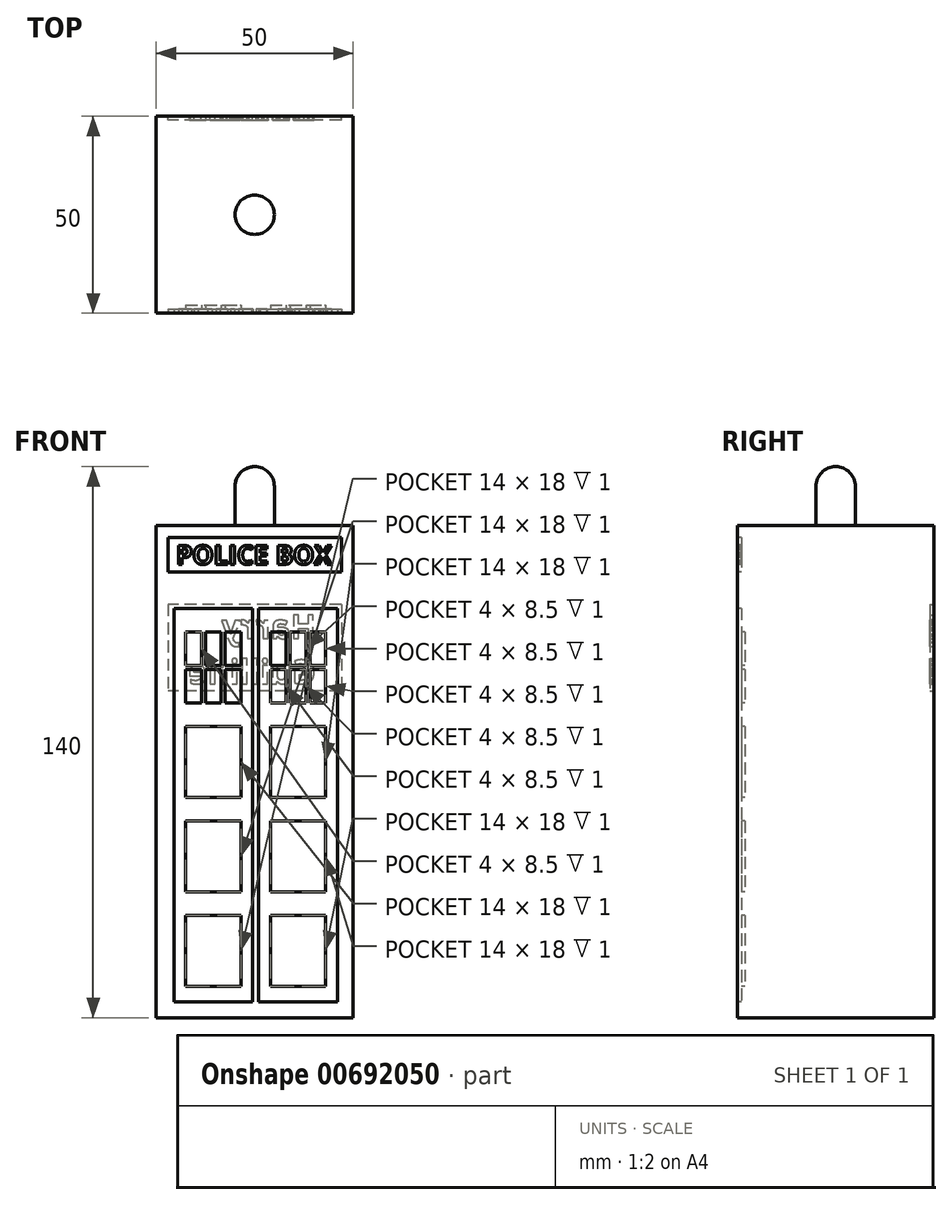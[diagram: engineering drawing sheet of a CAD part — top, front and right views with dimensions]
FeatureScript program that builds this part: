
annotation { "Feature Type Name" : "Feature", "Feature Type Description" : "" }
export const myFeature = defineFeature(function(context is Context, id is Id, definition is map)
    precondition{}
    {
        {
            var Q0;
            Q0=qCreatedBy(makeId("Top.planeOp"),FACE);
            var sketch = newSketch(context, id + "F0", { "sketchPlane" : qUnion([Q0])});
            skLineSegment(sketch, "E0.bottom", {"start": v(-25, 25) * mm, "end": v(25, 25) * mm});
            skLineSegment(sketch, "E0.top", {"start": v(-25, -25) * mm, "end": v(25, -25) * mm});
            skLineSegment(sketch, "E0.left", {"start": v(-25, 25) * mm, "end": v(-25, -25) * mm});
            skLineSegment(sketch, "E0.right", {"start": v(25, 25) * mm, "end": v(25, -25) * mm});
            skSolve(sketch);
        }
        {
            var Q0;
            Q0 = qSketchRegion(id + "F0", true);
            extrude(context, id + "F1", {"entities" : qUnion([Q0]), "depth" : 125 * mm, "offsetDistance" : 25 * mm});
        }
        {
            var Q0;
            Q0=makeQuery(id+"F1.opExtrude","CAP_FACE",FACE,{"disambiguationData":[OSD([sQuery(id+"F0.wireOp",EDGE,"E0.bottom"),sQuery(id+"F0.wireOp",EDGE,"E0.top"),sQuery(id+"F0.wireOp",EDGE,"E0.left"),sQuery(id+"F0.wireOp",EDGE,"E0.right")])],"isStart":false});
            cPlane(context, id + "F2", {"entities" : qUnion([Q0]), "cplaneType" : CPlaneType.OFFSET, "offset" : 0 * mm, "width" : 150 * mm, "height" : 150 * mm});
        }
        {
            var Q0;
            Q0=qCreatedBy(makeId("Front.planeOp"),FACE);
            var sketch = newSketch(context, id + "F3", { "sketchPlane" : qUnion([Q0])});
            skLineSegment(sketch, "E1", {"start": v(0, -12.11) * mm, "end": v(0, 144.87) * mm, "construction": true});
            skArc(sketch, "E2", {"start": v(0, 140) * mm, "mid": v(-3.54, 138.54) * mm, "end": v(-5, 135) * mm});
            skLineSegment(sketch, "E3.0.0", {"start": v(-25, 0) * mm, "end": v(25, 0) * mm});
            skLineSegment(sketch, "E3.0.1", {"start": v(25, 0) * mm, "end": v(25, 125) * mm});
            skLineSegment(sketch, "E3.0.2", {"start": v(25, 125) * mm, "end": v(-25, 125) * mm});
            skLineSegment(sketch, "E3.0.3", {"start": v(-25, 125) * mm, "end": v(-25, 0) * mm});
            skLineSegment(sketch, "E4", {"start": v(-5, 135) * mm, "end": v(-5, 125) * mm});
            skLineSegment(sketch, "E5", {"start": v(0, 140) * mm, "end": v(0, 125) * mm});
            skSolve(sketch);
        }
        {
            var Q0;
            Q0=makeQuery(id+"F3.imprint","IMPRINT",FACE,{"disambiguationData":[TD([[makeQuery(id+"F3.imprint","IMPRINT",EDGE,{"derivedFrom":sQuery(id+"F3.wireOp",EDGE,"E2")}),1.0]])]});
            var Q1;
            Q1=sQuery(id+"F3.wireOp",EDGE,"E1");
            revolve(context, id + "F4", {"operationType" : NewBodyOperationType.ADD, "entities" : qUnion([Q0]), "axis" : qUnion([Q1]), "revolveType" : RevolveType.FULL});
        }
        {
            var Q0;
            Q0=makeQuery(id+"F1.opExtrude","SWEPT_FACE",FACE,{"disambiguationData":[OSD([sQuery(id+"F0.wireOp",EDGE,"E0.top")])]});
            cPlane(context, id + "F5", {"entities" : qUnion([Q0]), "cplaneType" : CPlaneType.OFFSET, "offset" : 0 * mm, "width" : 150 * mm, "height" : 150 * mm});
        }
        {
            var Q0;
            Q0=qCreatedBy(id+"F5.planeOp",FACE);
            var sketch = newSketch(context, id + "F6", { "sketchPlane" : qUnion([Q0])});
            skLineSegment(sketch, "E6", {"start": v(0, -21.96) * mm, "end": v(0, 160.1) * mm, "construction": true});
            skLineSegment(sketch, "E7.bottom", {"start": v(-22, 122) * mm, "end": v(22, 122) * mm});
            skLineSegment(sketch, "E7.top", {"start": v(-22, 113.18) * mm, "end": v(22, 113.18) * mm});
            skLineSegment(sketch, "E7.left", {"start": v(-22, 122) * mm, "end": v(-22, 113.18) * mm});
            skLineSegment(sketch, "E7.right", {"start": v(22, 122) * mm, "end": v(22, 113.18) * mm});
            skLineSegment(sketch, "E8.0", {"start": v(-25, 125) * mm, "end": v(-25, 0) * mm});
            skLineSegment(sketch, "E9.0", {"start": v(-25, 125) * mm, "end": v(25, 125) * mm});
            skLineSegment(sketch, "E10.0", {"start": v(25, 125) * mm, "end": v(25, 0) * mm});
            skText(sketch, "E11", { "text": "POLICE BOX", "fontName": "OpenSans-Bold.ttf"});
            skLineSegment(sketch, "E12.bottom", {"start": v(1, 104) * mm, "end": v(21, 104) * mm});
            skLineSegment(sketch, "E12.top", {"start": v(1, 4) * mm, "end": v(21, 4) * mm});
            skLineSegment(sketch, "E12.left", {"start": v(1, 104) * mm, "end": v(1, 4) * mm});
            skLineSegment(sketch, "E12.right", {"start": v(21, 104) * mm, "end": v(21, 4) * mm});
            skLineSegment(sketch, "E13.bottom", {"start": v(4, 98) * mm, "end": v(18, 98) * mm});
            skLineSegment(sketch, "E13.top", {"start": v(4, 80) * mm, "end": v(18, 80) * mm});
            skLineSegment(sketch, "E13.left", {"start": v(4, 98) * mm, "end": v(4, 80) * mm});
            skLineSegment(sketch, "E13.right", {"start": v(18, 98) * mm, "end": v(18, 80) * mm});
            skLineSegment(sketch, "E14.bottom", {"start": v(4, 74) * mm, "end": v(18, 74) * mm});
            skLineSegment(sketch, "E14.top", {"start": v(4, 56) * mm, "end": v(18, 56) * mm});
            skLineSegment(sketch, "E14.left", {"start": v(4, 74) * mm, "end": v(4, 56) * mm});
            skLineSegment(sketch, "E14.right", {"start": v(18, 74) * mm, "end": v(18, 56) * mm});
            skLineSegment(sketch, "E15.bottom", {"start": v(4, 50) * mm, "end": v(18, 50) * mm});
            skLineSegment(sketch, "E15.top", {"start": v(4, 32) * mm, "end": v(18, 32) * mm});
            skLineSegment(sketch, "E15.left", {"start": v(4, 50) * mm, "end": v(4, 32) * mm});
            skLineSegment(sketch, "E15.right", {"start": v(18, 50) * mm, "end": v(18, 32) * mm});
            skLineSegment(sketch, "E16.bottom", {"start": v(4, 26) * mm, "end": v(18, 26) * mm});
            skLineSegment(sketch, "E16.top", {"start": v(4, 8) * mm, "end": v(18, 8) * mm});
            skLineSegment(sketch, "E16.left", {"start": v(4, 26) * mm, "end": v(4, 8) * mm});
            skLineSegment(sketch, "E16.right", {"start": v(18, 26) * mm, "end": v(18, 8) * mm});
            skLineSegment(sketch, "E17", {"start": v(4, 89.5) * mm, "end": v(8, 89.5) * mm});
            skLineSegment(sketch, "E18", {"start": v(4, 88.5) * mm, "end": v(8, 88.5) * mm});
            skLineSegment(sketch, "E19", {"start": v(8, 98) * mm, "end": v(8, 89.5) * mm});
            skLineSegment(sketch, "E20", {"start": v(9, 98) * mm, "end": v(9, 89.5) * mm});
            skLineSegment(sketch, "E21", {"start": v(13, 98) * mm, "end": v(13, 89.5) * mm});
            skLineSegment(sketch, "E22", {"start": v(14, 98) * mm, "end": v(14, 89.5) * mm});
            skLineSegment(sketch, "E23.trimOffspring", {"start": v(9, 88.5) * mm, "end": v(13, 88.5) * mm});
            skLineSegment(sketch, "E24.trimOffspring", {"start": v(9, 89.5) * mm, "end": v(13, 89.5) * mm});
            skLineSegment(sketch, "E25.trimOffspring", {"start": v(8, 88.5) * mm, "end": v(8, 80) * mm});
            skLineSegment(sketch, "E26.trimOffspring", {"start": v(9, 88.5) * mm, "end": v(9, 80) * mm});
            skLineSegment(sketch, "E27.trimOffspring", {"start": v(13, 88.5) * mm, "end": v(13, 80) * mm});
            skLineSegment(sketch, "E28.trimOffspring", {"start": v(14, 88.5) * mm, "end": v(14, 80) * mm});
            skLineSegment(sketch, "E29.trimOffspring", {"start": v(14, 89.5) * mm, "end": v(18, 89.5) * mm});
            skLineSegment(sketch, "E30.trimOffspring", {"start": v(14, 88.5) * mm, "end": v(18, 88.5) * mm});
            skLineSegment(sketch, "E31", {"start": v(-21.5, -74.33) * mm, "end": v(-21.5, 107.73) * mm, "construction": true});
            skLineSegment(sketch, "E32.bottom", {"start": v(-20.5, 104) * mm, "end": v(-0.5, 104) * mm});
            skLineSegment(sketch, "E32.top", {"start": v(-20.5, 4) * mm, "end": v(-0.5, 4) * mm});
            skLineSegment(sketch, "E32.left", {"start": v(-20.5, 104) * mm, "end": v(-20.5, 4) * mm});
            skLineSegment(sketch, "E32.right", {"start": v(-0.5, 104) * mm, "end": v(-0.5, 4) * mm});
            skLineSegment(sketch, "E33.bottom", {"start": v(-17.5, 98) * mm, "end": v(-3.5, 98) * mm});
            skLineSegment(sketch, "E33.top", {"start": v(-17.5, 80) * mm, "end": v(-3.5, 80) * mm});
            skLineSegment(sketch, "E33.left", {"start": v(-17.5, 98) * mm, "end": v(-17.5, 80) * mm});
            skLineSegment(sketch, "E33.right", {"start": v(-3.5, 98) * mm, "end": v(-3.5, 80) * mm});
            skLineSegment(sketch, "E34.bottom", {"start": v(-17.5, 74) * mm, "end": v(-3.5, 74) * mm});
            skLineSegment(sketch, "E34.top", {"start": v(-17.5, 56) * mm, "end": v(-3.5, 56) * mm});
            skLineSegment(sketch, "E34.left", {"start": v(-17.5, 74) * mm, "end": v(-17.5, 56) * mm});
            skLineSegment(sketch, "E34.right", {"start": v(-3.5, 74) * mm, "end": v(-3.5, 56) * mm});
            skLineSegment(sketch, "E35.bottom", {"start": v(-17.5, 50) * mm, "end": v(-3.5, 50) * mm});
            skLineSegment(sketch, "E35.top", {"start": v(-17.5, 32) * mm, "end": v(-3.5, 32) * mm});
            skLineSegment(sketch, "E35.left", {"start": v(-17.5, 50) * mm, "end": v(-17.5, 32) * mm});
            skLineSegment(sketch, "E35.right", {"start": v(-3.5, 50) * mm, "end": v(-3.5, 32) * mm});
            skLineSegment(sketch, "E36.bottom", {"start": v(-17.5, 26) * mm, "end": v(-3.5, 26) * mm});
            skLineSegment(sketch, "E36.top", {"start": v(-17.5, 8) * mm, "end": v(-3.5, 8) * mm});
            skLineSegment(sketch, "E36.left", {"start": v(-17.5, 26) * mm, "end": v(-17.5, 8) * mm});
            skLineSegment(sketch, "E36.right", {"start": v(-3.5, 26) * mm, "end": v(-3.5, 8) * mm});
            skLineSegment(sketch, "E37", {"start": v(-17.5, 89.5) * mm, "end": v(-13.5, 89.5) * mm});
            skLineSegment(sketch, "E38", {"start": v(-17.5, 88.5) * mm, "end": v(-13.5, 88.5) * mm});
            skLineSegment(sketch, "E39", {"start": v(-13.5, 98) * mm, "end": v(-13.5, 89.5) * mm});
            skLineSegment(sketch, "E40", {"start": v(-12.5, 98) * mm, "end": v(-12.5, 89.5) * mm});
            skLineSegment(sketch, "E41", {"start": v(-8.5, 98) * mm, "end": v(-8.5, 89.5) * mm});
            skLineSegment(sketch, "E42", {"start": v(-7.5, 98) * mm, "end": v(-7.5, 89.5) * mm});
            skLineSegment(sketch, "E43.trimOffspring", {"start": v(-12.5, 88.5) * mm, "end": v(-8.5, 88.5) * mm});
            skLineSegment(sketch, "E44.trimOffspring", {"start": v(-12.5, 89.5) * mm, "end": v(-8.5, 89.5) * mm});
            skLineSegment(sketch, "E45.trimOffspring", {"start": v(-13.5, 88.5) * mm, "end": v(-13.5, 80) * mm});
            skLineSegment(sketch, "E46.trimOffspring", {"start": v(-12.5, 88.5) * mm, "end": v(-12.5, 80) * mm});
            skLineSegment(sketch, "E47.trimOffspring", {"start": v(-8.5, 88.5) * mm, "end": v(-8.5, 80) * mm});
            skLineSegment(sketch, "E48.trimOffspring", {"start": v(-7.5, 88.5) * mm, "end": v(-7.5, 80) * mm});
            skLineSegment(sketch, "E49.trimOffspring", {"start": v(-7.5, 89.5) * mm, "end": v(-3.5, 89.5) * mm});
            skLineSegment(sketch, "E50.trimOffspring", {"start": v(-7.5, 88.5) * mm, "end": v(-3.5, 88.5) * mm});
            const initialGuessF6  = {"E11": [-0.02, 0.11518, 1, 0, 0.00482]};
            skSetInitialGuess(sketch, initialGuessF6);
            skSolve(sketch);
        }
        {
            var Q0;
            Q0=makeQuery(id+"F6.imprint","IMPRINT",FACE,{"disambiguationData":[TD([[makeQuery(id+"F6.imprint","IMPRINT",EDGE,{"derivedFrom":sQuery(id+"F6.wireOp",EDGE,"E7.bottom")}),-1.0]])]});
            var Q1;
            Q1=makeQuery(id+"F6.imprint","IMPRINT",FACE,{"disambiguationData":[TD([[makeQuery(id+"F6.imprint","IMPRINT",EDGE,{"derivedFrom":sQuery(id+"F6.wireOp",EDGE,"E11.sketch_text.stroke-24")}),1.0]])]});
            var Q2;
            Q2=makeQuery(id+"F6.imprint","IMPRINT",FACE,{"disambiguationData":[TD([[makeQuery(id+"F6.imprint","IMPRINT",EDGE,{"derivedFrom":sQuery(id+"F6.wireOp",EDGE,"E11.sketch_text.stroke-0")}),1.0]])]});
            var Q3;
            Q3=makeQuery(id+"F6.imprint","IMPRINT",FACE,{"disambiguationData":[TD([[makeQuery(id+"F6.imprint","IMPRINT",EDGE,{"derivedFrom":sQuery(id+"F6.wireOp",EDGE,"E11.sketch_text.stroke-100")}),1.0]])]});
            var Q4;
            Q4=makeQuery(id+"F6.imprint","IMPRINT",FACE,{"disambiguationData":[TD([[makeQuery(id+"F6.imprint","IMPRINT",EDGE,{"derivedFrom":sQuery(id+"F6.wireOp",EDGE,"E11.sketch_text.stroke-79")}),1.0]])]});
            var Q5;
            Q5=makeQuery(id+"F6.imprint","IMPRINT",FACE,{"disambiguationData":[TD([[makeQuery(id+"F6.imprint","IMPRINT",EDGE,{"derivedFrom":sQuery(id+"F6.wireOp",EDGE,"E11.sketch_text.stroke-86")}),1.0]])]});
            extrude(context, id + "F7", {"entities" : qUnion([Q0, Q1, Q2, Q3, Q4, Q5]), "operationType" : NewBodyOperationType.REMOVE, "oppositeDirection" : true, "depth" : 1 * mm, "offsetDistance" : 25 * mm});
        }
        {
            var Q0;
            {var subQ4=sQuery(id+"F6.wireOp",EDGE,"E37");Q0=makeQuery(id+"F6.imprint","IMPRINT",FACE,{"disambiguationData":[TD([[makeQuery(id+"F6.imprint","IMPRINT",EDGE,{"derivedFrom":subQ4}),1.0]])]});}
            var Q1;
            {var subQ0=sQuery(id+"F6.wireOp",EDGE,"E40");Q1=makeQuery(id+"F6.imprint","IMPRINT",FACE,{"disambiguationData":[TD([[makeQuery(id+"F6.imprint","IMPRINT",EDGE,{"derivedFrom":subQ0}),1.0]])]});}
            var Q2;
            {var subQ3=sQuery(id+"F6.wireOp",EDGE,"E42");Q2=makeQuery(id+"F6.imprint","IMPRINT",FACE,{"disambiguationData":[TD([[makeQuery(id+"F6.imprint","IMPRINT",EDGE,{"derivedFrom":subQ3}),1.0]])]});}
            var Q3;
            {var subQ4=sQuery(id+"F6.wireOp",EDGE,"E17");Q3=makeQuery(id+"F6.imprint","IMPRINT",FACE,{"disambiguationData":[TD([[makeQuery(id+"F6.imprint","IMPRINT",EDGE,{"derivedFrom":subQ4}),1.0]])]});}
            var Q4;
            {var subQ0=sQuery(id+"F6.wireOp",EDGE,"E20");Q4=makeQuery(id+"F6.imprint","IMPRINT",FACE,{"disambiguationData":[TD([[makeQuery(id+"F6.imprint","IMPRINT",EDGE,{"derivedFrom":subQ0}),1.0]])]});}
            var Q5;
            {var subQ3=sQuery(id+"F6.wireOp",EDGE,"E22");Q5=makeQuery(id+"F6.imprint","IMPRINT",FACE,{"disambiguationData":[TD([[makeQuery(id+"F6.imprint","IMPRINT",EDGE,{"derivedFrom":subQ3}),1.0]])]});}
            var Q6;
            {var subQ3=sQuery(id+"F6.wireOp",EDGE,"E28.trimOffspring");Q6=makeQuery(id+"F6.imprint","IMPRINT",FACE,{"disambiguationData":[TD([[makeQuery(id+"F6.imprint","IMPRINT",EDGE,{"derivedFrom":subQ3}),1.0]])]});}
            var Q7;
            Q7=makeQuery(id+"F6.imprint","IMPRINT",FACE,{"disambiguationData":[TD([[makeQuery(id+"F6.imprint","IMPRINT",EDGE,{"derivedFrom":sQuery(id+"F6.wireOp",EDGE,"E23.trimOffspring")}),-1.0]])]});
            var Q8;
            {var subQ4=sQuery(id+"F6.wireOp",EDGE,"E18");Q8=makeQuery(id+"F6.imprint","IMPRINT",FACE,{"disambiguationData":[TD([[makeQuery(id+"F6.imprint","IMPRINT",EDGE,{"derivedFrom":subQ4}),-1.0]])]});}
            var Q9;
            {var subQ3=sQuery(id+"F6.wireOp",EDGE,"E48.trimOffspring");Q9=makeQuery(id+"F6.imprint","IMPRINT",FACE,{"disambiguationData":[TD([[makeQuery(id+"F6.imprint","IMPRINT",EDGE,{"derivedFrom":subQ3}),1.0]])]});}
            var Q10;
            Q10=makeQuery(id+"F6.imprint","IMPRINT",FACE,{"disambiguationData":[TD([[makeQuery(id+"F6.imprint","IMPRINT",EDGE,{"derivedFrom":sQuery(id+"F6.wireOp",EDGE,"E43.trimOffspring")}),-1.0]])]});
            var Q11;
            {var subQ4=sQuery(id+"F6.wireOp",EDGE,"E38");Q11=makeQuery(id+"F6.imprint","IMPRINT",FACE,{"disambiguationData":[TD([[makeQuery(id+"F6.imprint","IMPRINT",EDGE,{"derivedFrom":subQ4}),-1.0]])]});}
            var Q12;
            Q12=makeQuery(id+"F6.imprint","IMPRINT",FACE,{"disambiguationData":[TD([[makeQuery(id+"F6.imprint","IMPRINT",EDGE,{"derivedFrom":sQuery(id+"F6.wireOp",EDGE,"E34.bottom")}),-1.0]])]});
            var Q13;
            Q13=makeQuery(id+"F6.imprint","IMPRINT",FACE,{"disambiguationData":[TD([[makeQuery(id+"F6.imprint","IMPRINT",EDGE,{"derivedFrom":sQuery(id+"F6.wireOp",EDGE,"E14.bottom")}),-1.0]])]});
            var Q14;
            Q14=makeQuery(id+"F6.imprint","IMPRINT",FACE,{"disambiguationData":[TD([[makeQuery(id+"F6.imprint","IMPRINT",EDGE,{"derivedFrom":sQuery(id+"F6.wireOp",EDGE,"E35.bottom")}),-1.0]])]});
            var Q15;
            Q15=makeQuery(id+"F6.imprint","IMPRINT",FACE,{"disambiguationData":[TD([[makeQuery(id+"F6.imprint","IMPRINT",EDGE,{"derivedFrom":sQuery(id+"F6.wireOp",EDGE,"E15.bottom")}),-1.0]])]});
            var Q16;
            Q16=makeQuery(id+"F6.imprint","IMPRINT",FACE,{"disambiguationData":[TD([[makeQuery(id+"F6.imprint","IMPRINT",EDGE,{"derivedFrom":sQuery(id+"F6.wireOp",EDGE,"E36.bottom")}),-1.0]])]});
            var Q17;
            Q17=makeQuery(id+"F6.imprint","IMPRINT",FACE,{"disambiguationData":[TD([[makeQuery(id+"F6.imprint","IMPRINT",EDGE,{"derivedFrom":sQuery(id+"F6.wireOp",EDGE,"E16.bottom")}),-1.0]])]});
            extrude(context, id + "F8", {"entities" : qUnion([Q0, Q1, Q2, Q3, Q4, Q5, Q6, Q7, Q8, Q9, Q10, Q11, Q12, Q13, Q14, Q15, Q16, Q17]), "operationType" : NewBodyOperationType.REMOVE, "oppositeDirection" : true, "depth" : 2 * mm, "offsetDistance" : 25 * mm});
        }
        {
            var Q0;
            Q0=makeQuery(id+"F6.imprint","IMPRINT",FACE,{"disambiguationData":[TD([[makeQuery(id+"F6.imprint","IMPRINT",EDGE,{"derivedFrom":sQuery(id+"F6.wireOp",EDGE,"E32.bottom")}),-1.0]])]});
            var Q1;
            Q1=makeQuery(id+"F6.imprint","IMPRINT",FACE,{"disambiguationData":[TD([[makeQuery(id+"F6.imprint","IMPRINT",EDGE,{"derivedFrom":sQuery(id+"F6.wireOp",EDGE,"E12.bottom")}),-1.0]])]});
            var Q2;
            {var subQ7=sQuery(id+"F6.wireOp",EDGE,"E37");Q2=makeQuery(id+"F6.imprint","IMPRINT",FACE,{"disambiguationData":[TD([[makeQuery(id+"F6.imprint","IMPRINT",EDGE,{"derivedFrom":subQ7}),-1.0]])]});}
            var Q3;
            {var subQ7=sQuery(id+"F6.wireOp",EDGE,"E17");Q3=makeQuery(id+"F6.imprint","IMPRINT",FACE,{"disambiguationData":[TD([[makeQuery(id+"F6.imprint","IMPRINT",EDGE,{"derivedFrom":subQ7}),-1.0]])]});}
            extrude(context, id + "F9", {"entities" : qUnion([Q0, Q1, Q2, Q3]), "operationType" : NewBodyOperationType.REMOVE, "oppositeDirection" : true, "depth" : 1 * mm, "offsetDistance" : 25 * mm});
        }
        {
            var Q0;
            Q0=makeQuery(id+"F1.opExtrude","SWEPT_FACE",FACE,{"disambiguationData":[OSD([sQuery(id+"F0.wireOp",EDGE,"E0.bottom")])]});
            cPlane(context, id + "F10", {"entities" : qUnion([Q0]), "cplaneType" : CPlaneType.OFFSET, "offset" : 0 * mm, "width" : 150 * mm, "height" : 150 * mm});
        }
        {
            var Q0;
            Q0=qCreatedBy(id+"F10.planeOp",FACE);
            var sketch = newSketch(context, id + "F11", { "sketchPlane" : qUnion([Q0])});
            skText(sketch, "E51", { "text": "Harry\nGuilline", "fontName": "OpenSans-Bold.ttf"});
            skLineSegment(sketch, "E52.bottom", {"start": v(-22, 105) * mm, "end": v(22, 105) * mm});
            skLineSegment(sketch, "E52.top", {"start": v(-22, 83) * mm, "end": v(22, 83) * mm});
            skLineSegment(sketch, "E52.left", {"start": v(-22, 105) * mm, "end": v(-22, 83) * mm});
            skLineSegment(sketch, "E52.right", {"start": v(22, 105) * mm, "end": v(22, 83) * mm});
            const initialGuessF11  = {"E51": [-0.01556, 0.09632, 1, 0, 0.00608]};
            skSetInitialGuess(sketch, initialGuessF11);
            skSolve(sketch);
        }
        {
            var Q0;
            Q0=makeQuery(id+"F11.imprint","IMPRINT",FACE,{"disambiguationData":[TD([[makeQuery(id+"F11.imprint","IMPRINT",EDGE,{"derivedFrom":sQuery(id+"F11.wireOp",EDGE,"E51.sketch_text.stroke-0")}),1.0]])]});
            var Q1;
            Q1=makeQuery(id+"F11.imprint","IMPRINT",FACE,{"disambiguationData":[TD([[makeQuery(id+"F11.imprint","IMPRINT",EDGE,{"derivedFrom":sQuery(id+"F11.wireOp",EDGE,"E51.sketch_text.stroke-30")}),1.0]])]});
            var Q2;
            Q2 = qSketchRegion(id + "F11", true);
            var Q3;
            Q3=makeQuery(id+"F11.imprint","IMPRINT",FACE,{"disambiguationData":[TD([[makeQuery(id+"F11.imprint","IMPRINT",EDGE,{"derivedFrom":sQuery(id+"F11.wireOp",EDGE,"E51.sketch_text.stroke-159")}),1.0]])]});
            extrude(context, id + "F12", {"entities" : qUnion([Q0, Q1, Q2, Q3]), "operationType" : NewBodyOperationType.REMOVE, "oppositeDirection" : true, "depth" : 1 * mm, "offsetDistance" : 25 * mm});
        }
    });
